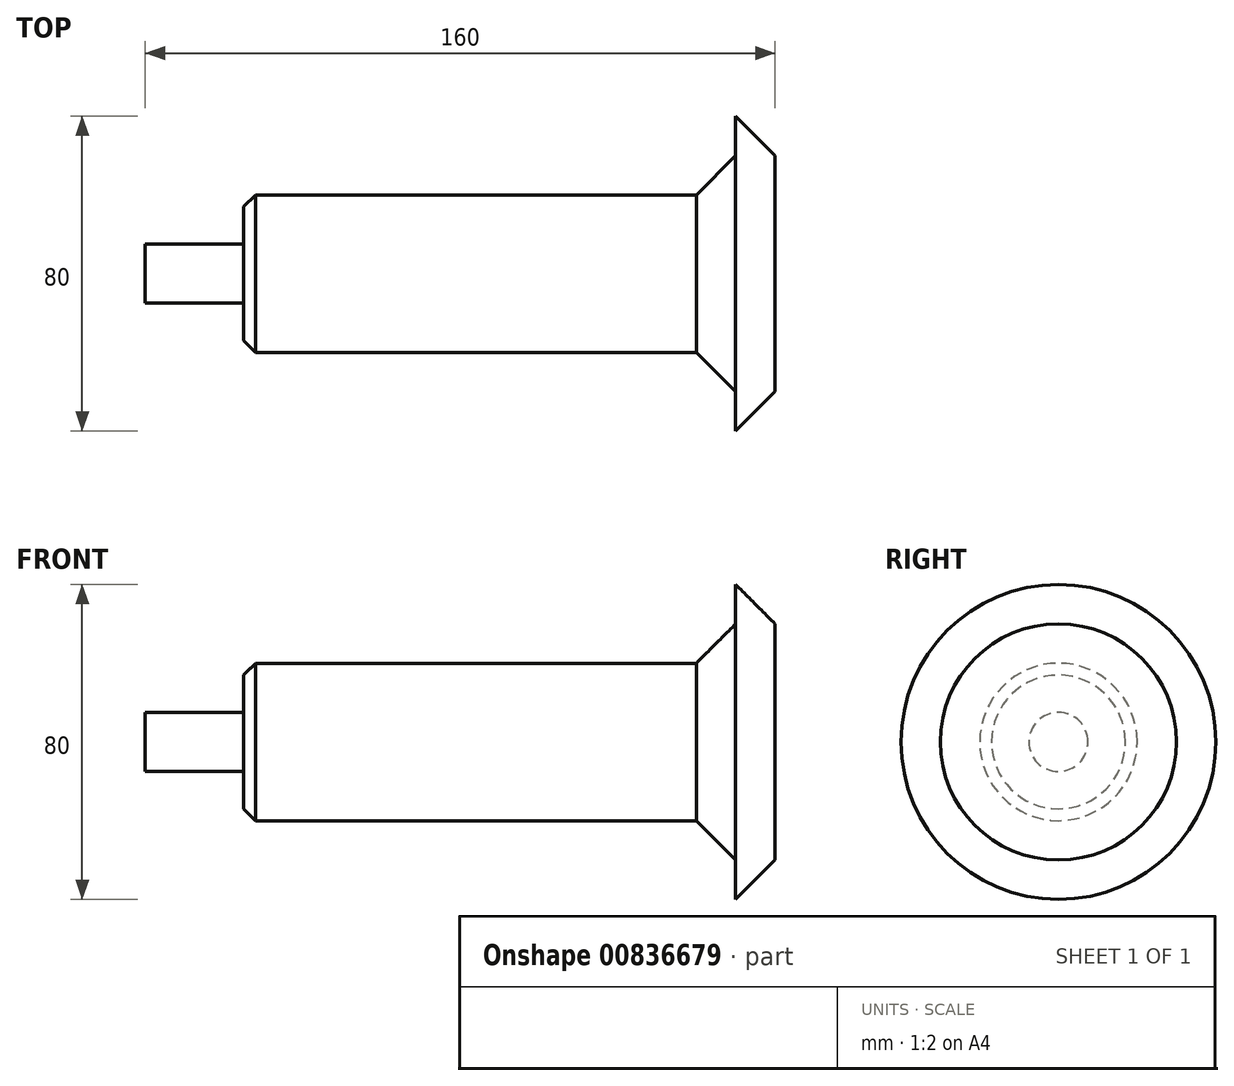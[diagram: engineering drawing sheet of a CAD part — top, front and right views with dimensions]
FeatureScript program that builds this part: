
annotation { "Feature Type Name" : "Feature", "Feature Type Description" : "" }
export const myFeature = defineFeature(function(context is Context, id is Id, definition is map)
    precondition{}
    {
        {
            var Q0;
            Q0=qCreatedBy(makeId("Top.planeOp"),FACE);
            var sketch = newSketch(context, id + "F0", { "sketchPlane" : qUnion([Q0])});
            skLineSegment(sketch, "E0.bottom", {"start": v(-66.81, 0) * mm, "end": v(-41.81, 0) * mm});
            skLineSegment(sketch, "E0.top", {"start": v(-66.81, 7.5) * mm, "end": v(-41.81, 7.5) * mm});
            skLineSegment(sketch, "E0.left", {"start": v(-66.81, 0) * mm, "end": v(-66.81, 7.5) * mm});
            skLineSegment(sketch, "E0.right", {"start": v(-41.81, 0) * mm, "end": v(-41.81, 7.5) * mm});
            skLineSegment(sketch, "E1.bottom", {"start": v(-41.81, 0) * mm, "end": v(73.19, 0) * mm});
            skLineSegment(sketch, "E1.top", {"start": v(-41.81, 20) * mm, "end": v(73.19, 20) * mm});
            skLineSegment(sketch, "E1.left", {"start": v(-41.81, 0) * mm, "end": v(-41.81, 20) * mm});
            skLineSegment(sketch, "E1.right", {"start": v(73.19, 0) * mm, "end": v(73.19, 20) * mm});
            skLineSegment(sketch, "E2.bottom", {"start": v(73.19, 0) * mm, "end": v(83.19, 0) * mm});
            skLineSegment(sketch, "E2.top", {"start": v(73.19, 30) * mm, "end": v(83.19, 30) * mm});
            skLineSegment(sketch, "E2.left", {"start": v(73.19, 0) * mm, "end": v(73.19, 30) * mm});
            skLineSegment(sketch, "E2.right", {"start": v(83.19, 0) * mm, "end": v(83.19, 30) * mm});
            skLineSegment(sketch, "E3.bottom", {"start": v(83.19, 0) * mm, "end": v(93.19, 0) * mm});
            skLineSegment(sketch, "E3.top", {"start": v(83.19, 40) * mm, "end": v(93.19, 40) * mm});
            skLineSegment(sketch, "E3.left", {"start": v(83.19, 0) * mm, "end": v(83.19, 40) * mm});
            skLineSegment(sketch, "E3.right", {"start": v(93.19, 0) * mm, "end": v(93.19, 40) * mm});
            skSolve(sketch);
        }
        {
            var Q0;
            {var subQ0=sQuery(id+"F0.wireOp",EDGE,"E0.bottom");Q0=makeQuery(id+"F0.imprint","IMPRINT",FACE,{"disambiguationData":[TD([[makeQuery(id+"F0.imprint","IMPRINT",EDGE,{"derivedFrom":subQ0}),1.0]])]});}
            var Q1;
            {var subQ3=sQuery(id+"F0.wireOp",EDGE,"E1.bottom");Q1=makeQuery(id+"F0.imprint","IMPRINT",FACE,{"disambiguationData":[TD([[makeQuery(id+"F0.imprint","IMPRINT",EDGE,{"derivedFrom":subQ3}),1.0]])]});}
            var Q2;
            {var subQ3=sQuery(id+"F0.wireOp",EDGE,"E2.bottom");Q2=makeQuery(id+"F0.imprint","IMPRINT",FACE,{"disambiguationData":[TD([[makeQuery(id+"F0.imprint","IMPRINT",EDGE,{"derivedFrom":subQ3}),1.0]])]});}
            var Q3;
            {var subQ3=sQuery(id+"F0.wireOp",EDGE,"E3.bottom");Q3=makeQuery(id+"F0.imprint","IMPRINT",FACE,{"disambiguationData":[TD([[makeQuery(id+"F0.imprint","IMPRINT",EDGE,{"derivedFrom":subQ3}),1.0]])]});}
            var Q4;
            Q4=sQuery(id+"F0.wireOp",EDGE,"E1.bottom");
            revolve(context, id + "F1", {"surfaceOperationType" : NewSurfaceOperationType.NEW, "entities" : qUnion([Q0, Q1, Q2, Q3]), "axis" : qUnion([Q4]), "revolveType" : RevolveType.FULL});
        }
        {
            var Q0;
            Q0=makeQuery(id+"F1.opRevolve","SWEPT_EDGE",EDGE,{"disambiguationData":[OSD([sQuery(id+"F0.wireOp",EDGE,"E1.top"),sQuery(id+"F0.wireOp",EDGE,"E1.left")])]});
            chamfer(context, id + "F2", {"entities" : qUnion([Q0]), "width" : 3 * mm, "tangentPropagation" : true});
        }
        {
            var Q0;
            Q0=makeQuery(id+"F1.opRevolve","SWEPT_EDGE",EDGE,{"disambiguationData":[OSD([sQuery(id+"F0.wireOp",EDGE,"E2.top"),sQuery(id+"F0.wireOp",EDGE,"E2.left")])]});
            chamfer(context, id + "F3", {"entities" : qUnion([Q0]), "width" : 10 * mm, "tangentPropagation" : true});
        }
        {
            var Q0;
            Q0=makeQuery(id+"F1.opRevolve","SWEPT_EDGE",EDGE,{"disambiguationData":[OSD([sQuery(id+"F0.wireOp",EDGE,"E3.top"),sQuery(id+"F0.wireOp",EDGE,"E3.right")])]});
            chamfer(context, id + "F4", {"entities" : qUnion([Q0]), "width" : 10 * mm, "tangentPropagation" : true});
        }
    });
